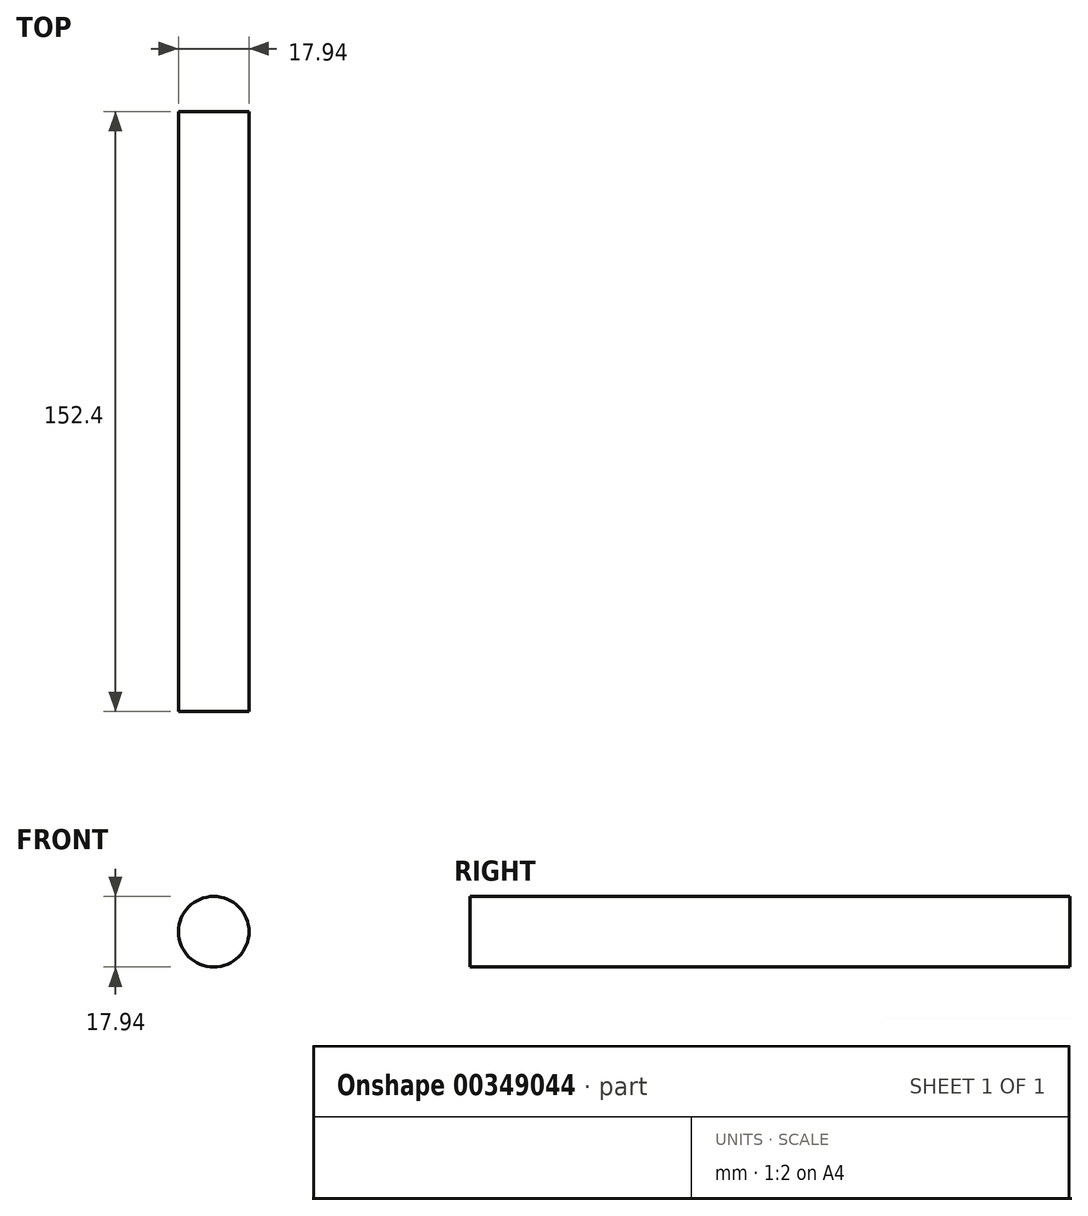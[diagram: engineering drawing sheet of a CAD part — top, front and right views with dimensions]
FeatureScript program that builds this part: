
annotation { "Feature Type Name" : "Feature", "Feature Type Description" : "" }
export const myFeature = defineFeature(function(context is Context, id is Id, definition is map)
    precondition{}
    {
        {
            var Q0;
            Q0=qCreatedBy(makeId("Front.planeOp"),FACE);
            var sketch = newSketch(context, id + "F0", { "sketchPlane" : qUnion([Q0])});
            skCircle(sketch, "E0", {"center": v(0, 0) * mm, "radius": 8.97 * mm});
            skSolve(sketch);
        }
        {
            var Q0;
            Q0=makeQuery(id+"F0.imprint","IMPRINT",FACE,{"disambiguationData":[TD([[makeQuery(id+"F0.imprint","IMPRINT",EDGE,{"derivedFrom":sQuery(id+"F0.wireOp",EDGE,"E0")}),1.0]])]});
            extrude(context, id + "F1", {"entities" : qUnion([Q0]), "endBound" : BoundingType.SYMMETRIC, "depth" : 152.4 * mm});
        }
    });
